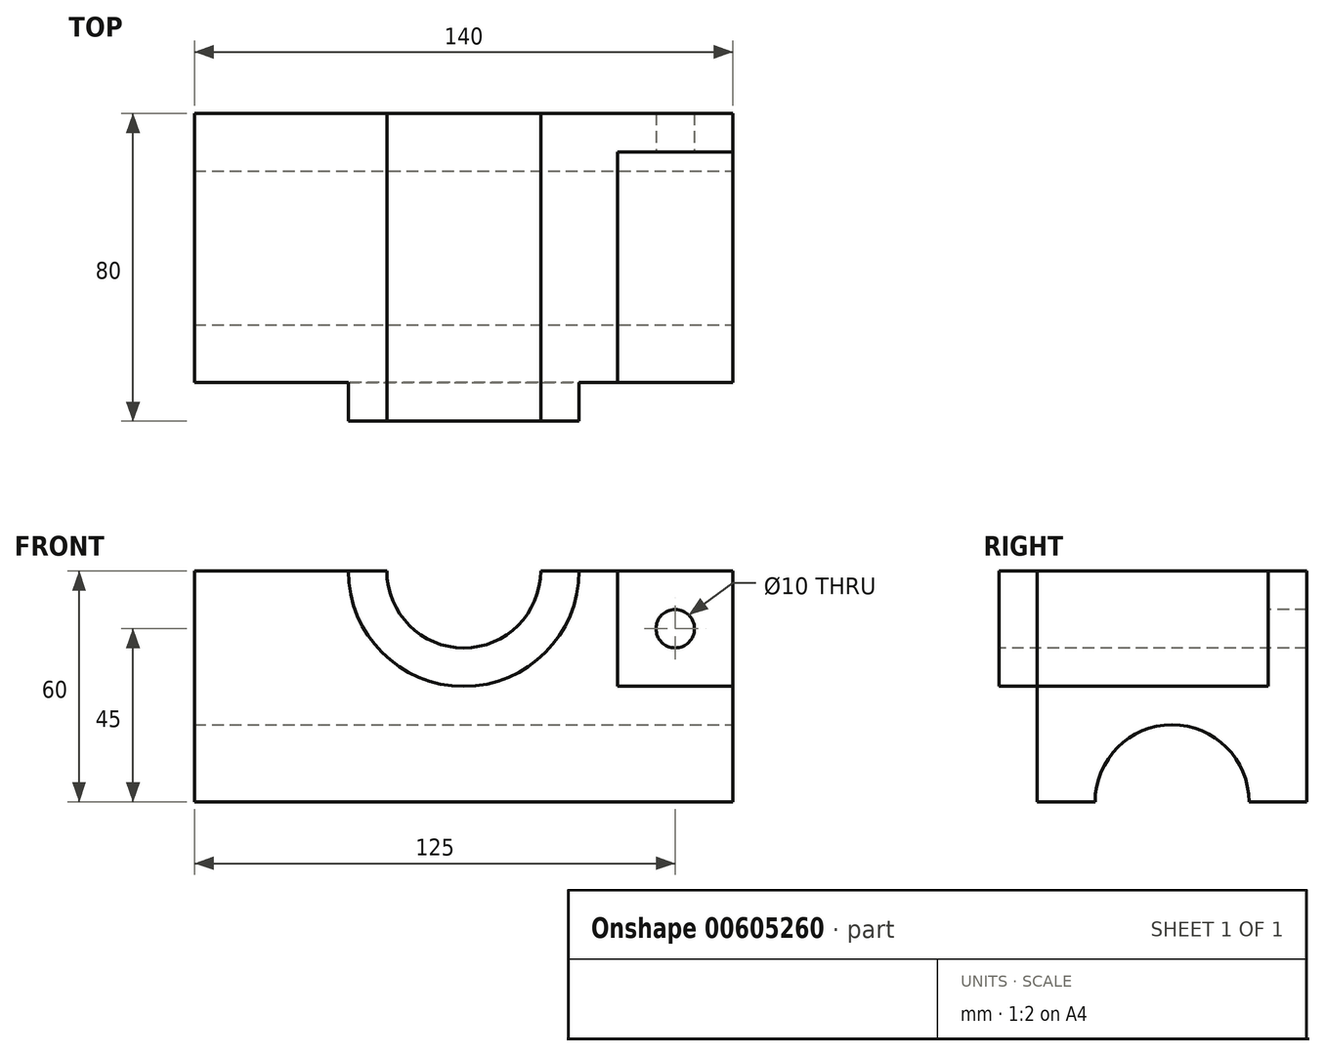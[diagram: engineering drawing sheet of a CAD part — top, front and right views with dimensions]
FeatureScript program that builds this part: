
annotation { "Feature Type Name" : "Feature", "Feature Type Description" : "" }
export const myFeature = defineFeature(function(context is Context, id is Id, definition is map)
    precondition{}
    {
        {
            var Q0;
            Q0=qCreatedBy(makeId("Front.planeOp"),FACE);
            var sketch = newSketch(context, id + "F0", { "sketchPlane" : qUnion([Q0])});
            skLineSegment(sketch, "E0.bottom", {"start": v(70, -30) * mm, "end": v(-70, -30) * mm});
            skLineSegment(sketch, "E0.top", {"start": v(70, 30) * mm, "end": v(-70, 30) * mm});
            skLineSegment(sketch, "E0.left", {"start": v(70, -30) * mm, "end": v(70, 30) * mm});
            skLineSegment(sketch, "E0.right", {"start": v(-70, -30) * mm, "end": v(-70, 30) * mm});
            skPoint(sketch, "E0.middle", {"position": v(0, 0) * mm});
            skSolve(sketch);
        }
        {
            var Q0;
            Q0=makeQuery(id+"F0.imprint","IMPRINT",FACE,{"disambiguationData":[TD([[makeQuery(id+"F0.imprint","IMPRINT",EDGE,{"derivedFrom":sQuery(id+"F0.wireOp",EDGE,"E0.bottom")}),-1.0]])]});
            extrude(context, id + "F1", {"entities" : qUnion([Q0]), "oppositeDirection" : true, "depth" : 70 * mm, "offsetDistance" : 25 * mm});
        }
        {
            var Q0;
            Q0=makeQuery(id+"F1.opExtrude","CAP_FACE",FACE,{"disambiguationData":[OSD([sQuery(id+"F0.wireOp",EDGE,"E0.bottom"),sQuery(id+"F0.wireOp",EDGE,"E0.top"),sQuery(id+"F0.wireOp",EDGE,"E0.left"),sQuery(id+"F0.wireOp",EDGE,"E0.right")])],"isStart":true});
            var sketch = newSketch(context, id + "F2", { "sketchPlane" : qUnion([Q0])});
            skArc(sketch, "E1", {"start": v(-20, 30) * mm, "mid": v(0, 10) * mm, "end": v(20, 30) * mm});
            skLineSegment(sketch, "E2", {"start": v(-20, 30) * mm, "end": v(20, 30) * mm});
            skSolve(sketch);
        }
        {
            var Q0;
            Q0=makeQuery(id+"F2.imprint","IMPRINT",FACE,{"disambiguationData":[TD([[makeQuery(id+"F2.imprint","IMPRINT",EDGE,{"derivedFrom":sQuery(id+"F2.wireOp",EDGE,"E1")}),1.0]])]});
            var Q1;
            Q1=makeQuery(id+"F1.opExtrude","CAP_FACE",FACE,{"disambiguationData":[OSD([sQuery(id+"F0.wireOp",EDGE,"E0.bottom"),sQuery(id+"F0.wireOp",EDGE,"E0.top"),sQuery(id+"F0.wireOp",EDGE,"E0.left"),sQuery(id+"F0.wireOp",EDGE,"E0.right")])],"isStart":false});
            extrude(context, id + "F3", {"entities" : qUnion([Q0]), "operationType" : NewBodyOperationType.REMOVE, "endBound" : BoundingType.UP_TO_SURFACE, "oppositeDirection" : true, "depth" : 25 * mm, "endBoundEntityFace" : qUnion([Q1]), "offsetDistance" : 25 * mm});
        }
        {
            var Q0;
            Q0=makeQuery(id+"F1.opExtrude","CAP_FACE",FACE,{"disambiguationData":[OSD([sQuery(id+"F0.wireOp",EDGE,"E0.bottom"),sQuery(id+"F0.wireOp",EDGE,"E0.top"),sQuery(id+"F0.wireOp",EDGE,"E0.left"),sQuery(id+"F0.wireOp",EDGE,"E0.right")])],"isStart":true});
            var sketch = newSketch(context, id + "F4", { "sketchPlane" : qUnion([Q0])});
            skLineSegment(sketch, "E3", {"start": v(70, 0) * mm, "end": v(40, 0) * mm});
            skLineSegment(sketch, "E4", {"start": v(40, 0) * mm, "end": v(40, 30) * mm});
            skSolve(sketch);
        }
        {
            var Q0;
            {var subQ0=sQuery(id+"F4.wireOp",EDGE,"E3");Q0=makeQuery(id+"F4.imprint","IMPRINT",FACE,{"disambiguationData":[TD([[makeQuery(id+"F4.imprint","IMPRINT",EDGE,{"derivedFrom":subQ0}),-1.0]])]});}
            extrude(context, id + "F5", {"entities" : qUnion([Q0]), "operationType" : NewBodyOperationType.REMOVE, "oppositeDirection" : true, "depth" : 60 * mm, "offsetDistance" : 25 * mm});
        }
        {
            var Q0;
            Q0=makeQuery(id+"F5.boolean.opBoolean","COPY",FACE,{"derivedFrom":makeQuery(id+"F5.opExtrude","CAP_FACE",FACE,{"disambiguationData":[OSD([sQuery(id+"F0.wireOp",EDGE,"E0.top"),sQuery(id+"F0.wireOp",EDGE,"E0.left"),sQuery(id+"F4.wireOp",EDGE,"E3"),sQuery(id+"F4.wireOp",EDGE,"E4")])],"isStart":false})});
            var sketch = newSketch(context, id + "F6", { "sketchPlane" : qUnion([Q0])});
            skCircle(sketch, "E5", {"center": v(55, 15) * mm, "radius": 5 * mm});
            skPoint(sketch, "E5.centerSnap0", {"position": v(40, 15) * mm});
            skSolve(sketch);
        }
        {
            var Q0;
            Q0=makeQuery(id+"F6.imprint","IMPRINT",FACE,{"disambiguationData":[TD([[makeQuery(id+"F6.imprint","IMPRINT",EDGE,{"derivedFrom":sQuery(id+"F6.wireOp",EDGE,"E5")}),1.0]])]});
            var Q1;
            Q1=makeQuery(id+"F1.opExtrude","CAP_FACE",FACE,{"disambiguationData":[OSD([sQuery(id+"F0.wireOp",EDGE,"E0.bottom"),sQuery(id+"F0.wireOp",EDGE,"E0.top"),sQuery(id+"F0.wireOp",EDGE,"E0.left"),sQuery(id+"F0.wireOp",EDGE,"E0.right")])],"isStart":false});
            extrude(context, id + "F7", {"entities" : qUnion([Q0]), "operationType" : NewBodyOperationType.REMOVE, "endBound" : BoundingType.UP_TO_SURFACE, "oppositeDirection" : true, "depth" : 25 * mm, "endBoundEntityFace" : qUnion([Q1]), "offsetDistance" : 25 * mm});
        }
        {
            var Q0;
            Q0=makeQuery(id+"F1.opExtrude","SWEPT_FACE",FACE,{"disambiguationData":[OSD([sQuery(id+"F0.wireOp",EDGE,"E0.left")])]});
            var sketch = newSketch(context, id + "F8", { "sketchPlane" : qUnion([Q0])});
            skArc(sketch, "E6", {"start": v(55, -30) * mm, "mid": v(35, -10) * mm, "end": v(15, -30) * mm});
            skLineSegment(sketch, "E7", {"start": v(15, -30) * mm, "end": v(55, -30) * mm});
            skSolve(sketch);
        }
        {
            var Q0;
            Q0 = qSketchRegion(id + "F8", true);
            var Q1;
            Q1=makeQuery(id+"F1.opExtrude","SWEPT_FACE",FACE,{"disambiguationData":[OSD([sQuery(id+"F0.wireOp",EDGE,"E0.right")])]});
            extrude(context, id + "F9", {"entities" : qUnion([Q0]), "operationType" : NewBodyOperationType.REMOVE, "endBound" : BoundingType.UP_TO_SURFACE, "oppositeDirection" : true, "depth" : 25 * mm, "endBoundEntityFace" : qUnion([Q1]), "offsetDistance" : 25 * mm});
        }
        {
            var Q0;
            Q0=makeQuery(id+"F1.opExtrude","CAP_FACE",FACE,{"disambiguationData":[OSD([sQuery(id+"F0.wireOp",EDGE,"E0.bottom"),sQuery(id+"F0.wireOp",EDGE,"E0.top"),sQuery(id+"F0.wireOp",EDGE,"E0.left"),sQuery(id+"F0.wireOp",EDGE,"E0.right")])],"isStart":true});
            var sketch = newSketch(context, id + "F10", { "sketchPlane" : qUnion([Q0])});
            skArc(sketch, "E8.0", {"start": v(-30, 30) * mm, "mid": v(0, 0) * mm, "end": v(30, 30) * mm});
            skArc(sketch, "E9.0", {"start": v(-20, 30) * mm, "mid": v(0, 10) * mm, "end": v(20, 30) * mm});
            skLineSegment(sketch, "E10", {"start": v(-30, 30) * mm, "end": v(-20, 30) * mm});
            skLineSegment(sketch, "E11", {"start": v(20, 30) * mm, "end": v(30, 30) * mm});
            skSolve(sketch);
        }
        {
            var Q0;
            Q0=makeQuery(id+"F10.imprint","IMPRINT",FACE,{"disambiguationData":[TD([[makeQuery(id+"F10.imprint","IMPRINT",EDGE,{"derivedFrom":sQuery(id+"F10.wireOp",EDGE,"E8.0")}),1.0]])]});
            extrude(context, id + "F11", {"entities" : qUnion([Q0]), "operationType" : NewBodyOperationType.ADD, "depth" : 10 * mm, "offsetDistance" : 25 * mm});
        }
    });
